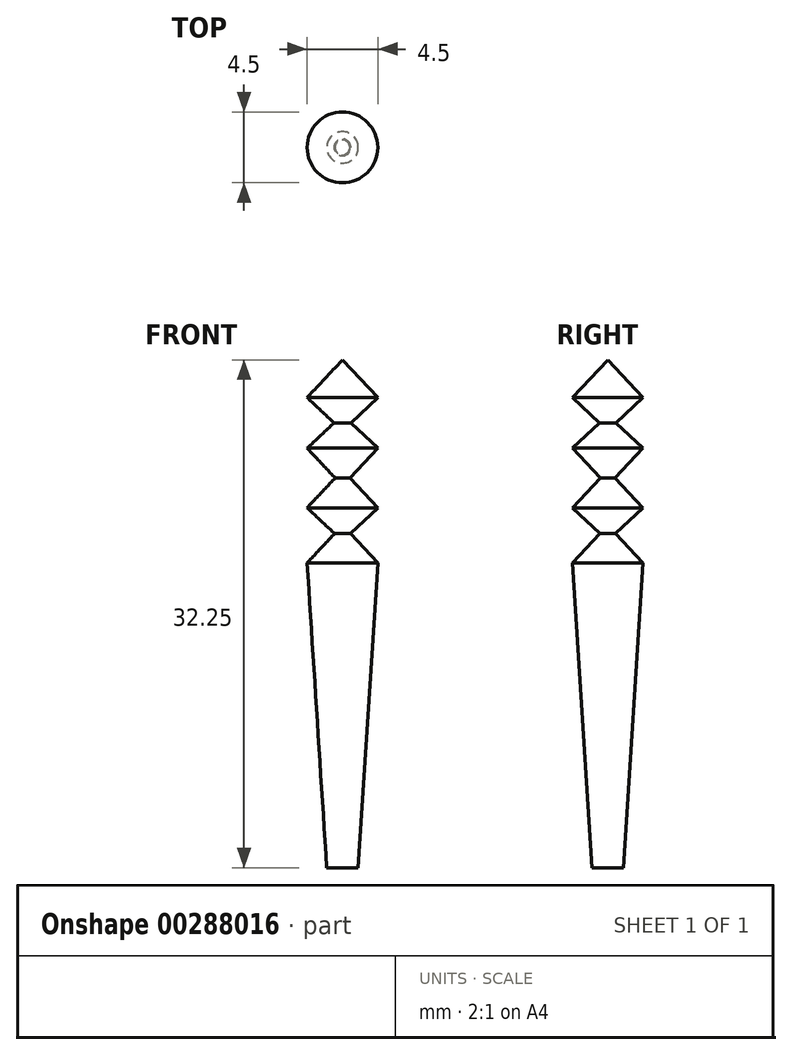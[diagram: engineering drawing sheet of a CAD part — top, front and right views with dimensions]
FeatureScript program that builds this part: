
annotation { "Feature Type Name" : "Feature", "Feature Type Description" : "" }
export const myFeature = defineFeature(function(context is Context, id is Id, definition is map)
    precondition{}
    {
        {
            var Q0;
            Q0=qCreatedBy(makeId("Front.planeOp"),FACE);
            var sketch = newSketch(context, id + "F0", { "sketchPlane" : qUnion([Q0])});
            skLineSegment(sketch, "E0", {"start": v(0, 0) * mm, "end": v(0, 30) * mm});
            skCircle(sketch, "E1", {"center": v(0, 30) * mm, "radius": 2.25 * mm, "construction": true});
            skCircle(sketch, "E2.1.0.0", {"center": v(0, 26.5) * mm, "radius": 2.25 * mm, "construction": true});
            skCircle(sketch, "E2.2.0.0", {"center": v(0, 23) * mm, "radius": 2.25 * mm, "construction": true});
            skCircle(sketch, "E2.3.0.0", {"center": v(0, 19.5) * mm, "radius": 2.25 * mm, "construction": true});
            skLineSegment(sketch, "E2.direction1", {"start": v(0, 30) * mm, "end": v(0, 26.5) * mm, "construction": true});
            skLineSegment(sketch, "E3", {"start": v(0, 0) * mm, "end": v(1, 0) * mm});
            skLineSegment(sketch, "E4", {"start": v(1, 0) * mm, "end": v(2.25, 19.36) * mm});
            skLineSegment(sketch, "E5", {"start": v(0, 30) * mm, "end": v(0, 32.25) * mm});
            skLineSegment(sketch, "E6", {"start": v(0, 32.25) * mm, "end": v(2.25, 29.86) * mm});
            skLineSegment(sketch, "E7", {"start": v(2.25, 29.86) * mm, "end": v(0, 27.75) * mm});
            skLineSegment(sketch, "E8", {"start": v(0, 28.75) * mm, "end": v(2.25, 26.64) * mm});
            skLineSegment(sketch, "E9", {"start": v(2.25, 26.64) * mm, "end": v(0, 24.25) * mm});
            skLineSegment(sketch, "E10", {"start": v(0, 25.25) * mm, "end": v(2.25, 22.86) * mm});
            skLineSegment(sketch, "E11", {"start": v(2.25, 22.86) * mm, "end": v(0, 20.75) * mm});
            skLineSegment(sketch, "E12", {"start": v(0, 21.75) * mm, "end": v(2.25, 19.36) * mm});
            skSolve(sketch);
        }
        {
            var Q0;
            {var subQ1=sQuery(id+"F0.wireOp",EDGE,"E5");Q0=makeQuery(id+"F0.imprint","IMPRINT",FACE,{"disambiguationData":[TD([[makeQuery(id+"F0.imprint","IMPRINT",EDGE,{"derivedFrom":subQ1}),-1.0]])]});}
            var Q1;
            {var subQ0=sQuery(id+"F0.wireOp",EDGE,"E7");var subQ1=sQuery(id+"F0.wireOp",EDGE,"E0");var subQ2=makeQuery(id+"F0.imprint","INTERSECT",VERTEX,{"derivedFrom":[subQ1,subQ0]});Q1=makeQuery(id+"F0.imprint","IMPRINT",FACE,{"disambiguationData":[TD([[makeQuery(id+"F0.imprint","IMPRINT",EDGE,{"disambiguationData":[TD([[subQ2,-1.0]])],"derivedFrom":subQ1}),-1.0]])]});}
            var Q2;
            {var subQ5=sQuery(id+"F0.wireOp",EDGE,"E7");var subQ6=sQuery(id+"F0.wireOp",EDGE,"E0");var subQ7=makeQuery(id+"F0.imprint","INTERSECT",VERTEX,{"derivedFrom":[subQ6,subQ5]});Q2=makeQuery(id+"F0.imprint","IMPRINT",FACE,{"disambiguationData":[TD([[makeQuery(id+"F0.imprint","IMPRINT",EDGE,{"disambiguationData":[TD([[subQ7,1.0]])],"derivedFrom":subQ6}),-1.0]])]});}
            var Q3;
            {var subQ0=sQuery(id+"F0.wireOp",EDGE,"E9");var subQ1=sQuery(id+"F0.wireOp",EDGE,"E0");var subQ2=makeQuery(id+"F0.imprint","INTERSECT",VERTEX,{"derivedFrom":[subQ1,subQ0]});Q3=makeQuery(id+"F0.imprint","IMPRINT",FACE,{"disambiguationData":[TD([[makeQuery(id+"F0.imprint","IMPRINT",EDGE,{"disambiguationData":[TD([[subQ2,-1.0]])],"derivedFrom":subQ1}),-1.0]])]});}
            var Q4;
            {var subQ5=sQuery(id+"F0.wireOp",EDGE,"E9");var subQ7=sQuery(id+"F0.wireOp",EDGE,"E0");var subQ8=makeQuery(id+"F0.imprint","INTERSECT",VERTEX,{"derivedFrom":[subQ7,subQ5]});Q4=makeQuery(id+"F0.imprint","IMPRINT",FACE,{"disambiguationData":[TD([[makeQuery(id+"F0.imprint","IMPRINT",EDGE,{"disambiguationData":[TD([[subQ8,1.0]])],"derivedFrom":subQ7}),-1.0]])]});}
            var Q5;
            {var subQ0=sQuery(id+"F0.wireOp",EDGE,"E11");var subQ1=sQuery(id+"F0.wireOp",EDGE,"E0");var subQ2=makeQuery(id+"F0.imprint","INTERSECT",VERTEX,{"derivedFrom":[subQ1,subQ0]});Q5=makeQuery(id+"F0.imprint","IMPRINT",FACE,{"disambiguationData":[TD([[makeQuery(id+"F0.imprint","IMPRINT",EDGE,{"disambiguationData":[TD([[subQ2,-1.0]])],"derivedFrom":subQ1}),-1.0]])]});}
            var Q6;
            {var subQ1=sQuery(id+"F0.wireOp",EDGE,"E3");Q6=makeQuery(id+"F0.imprint","IMPRINT",FACE,{"disambiguationData":[TD([[makeQuery(id+"F0.imprint","IMPRINT",EDGE,{"derivedFrom":subQ1}),1.0]])]});}
            var Q7;
            Q7=sQuery(id+"F0.wireOp",EDGE,"E0");
            revolve(context, id + "F1", {"entities" : qUnion([Q0, Q1, Q2, Q3, Q4, Q5, Q6]), "axis" : qUnion([Q7]), "revolveType" : RevolveType.FULL});
        }
    });
